# Revit family: Camera-Security-Panasonic-Dome-Network-S3111LSeriesX
name_source: partatom
category: Security Devices
revit_build: Autodesk Revit 2016 (Build: 20150220_1215(x64)
units: mm (PartAtom-declared; Revit-internal decimal feet)

## family parameters
Cut with Voids When Loaded = No
Host = Face
Maintain Annotation Orientation = No
OmniClass Number = 23.85.10.14.11
OmniClass Title = Cameras
Part Type = Normal
Room Calculation Point = No
Round Connector Dimension = Use Diameter
Shared = No

## types (2) — shared parameters
Audio In = No
Audio Out = No
Communication Ports = 10Base-T / 100Base-TX, RJ45 connector
Date Last Modified = 2019/01/16
Day Or Night = Yes
Diameter = 4.094 "
Dome Part Number = WV-CW6SA
Equipment Abbreviation = SC
Family Version = 1.0.0
Has POE = Yes
Height = 2.008 "
IP Or Analog = IP
Indoor Or Outdoor = Indoor
Manufacturer = Panasonic
Minimum Illumination = 0 lx
Model Disclaimer = Contact Panasonic for more information
Mounting Positions = Surface Mount
Operational Humidity = 10 to 90 % (no condensation)
Operational Temperature = 0 °C to +40 °C (32 °F to 104 °F)
Panning Range = ±45°
PoE = 48 V
Power Active = 3.8 W
Product Documentation Link = https://bizpartner.panasonic.net
Product Material = ABS Resin - Panasonic - Sail White
Product Page URL = https://security.panasonic.com
Provide Feedback = https://www.surveymonkey.com
Rated Current = 80 mA
Regulatory Compliance = UL (UL60950-1), c-UL (CSA C22.2 No.60950-1), CE, IEC60950-1,FCC (Part15 Subpart B, ClassA, SDoC), ICES-003 ClassA, EN55032 ClassB, EN55024
Storage Temperature = 32°F - 104°F
Tilting Range = 0 to +90°
URL = http://security.panasonic.com
Vandal Resistant = No
Weight = 0.66 lb
Wide Dynamic Range = Yes
z Base Radius = 2.047 "
z Const Pan Handle Length = 27.559 "
z Const Tilt Base Length = 9.843 "
z Const Tilt Base2 Length = 19.685 "
z Const Tilt Handle Length = 9.843 "
z Const Yaw Base Length = 10.236 "
z Const Yaw Base2 Length = 17.323 "
z Const Yaw Handle Length = 9.252 "
z Dome Material = Acrylic Resin - Panasonic - Clear
z Tilt Offset Length = 0.669 "
z VV Viewpoint Depth Max = 0.689 "
z VV Viewpoint Depth Min = 0.689 "
zero-valued in all types: Default Elevation

## per-type parameters (varying)
| type | Angle Of View | Description | HFOV Max 169 | HFOV Max 43 | HFOV Min 169 | HFOV Min 43 | Part Description | VFOV Max 169 | VFOV Max 43 | VFOV Min 169 | VFOV Min 43 | z Camera Resolution Type |
| WV-S3111L | 97 | Security Camera, Super Dynamic, HD, Dome, Network | 97.00° | 97.00° | 97.00° | 97.00° | Security Camera, Super Dynamic, HD, Dome, Network | 54.00° | 72.00° | 54.00° | 72.00° | 1 |
| WV-S3131L | 108 | Security Camera, Super Dynamic, FullHD, Dome, Network | 108.00° | 89.00° | 108.00° | 89.00° | Security Camera, Super Dynamic, FullHD, Dome, Network | 60.00° | 66.00° | 60.00° | 66.00° | 2 |

note: column(s) folded — value = type name in every type: Model, Part Number

## geometry (parser evidence)
native form markers: Blend x2, Sweep x5
no freeform markers — native parametric forms only
